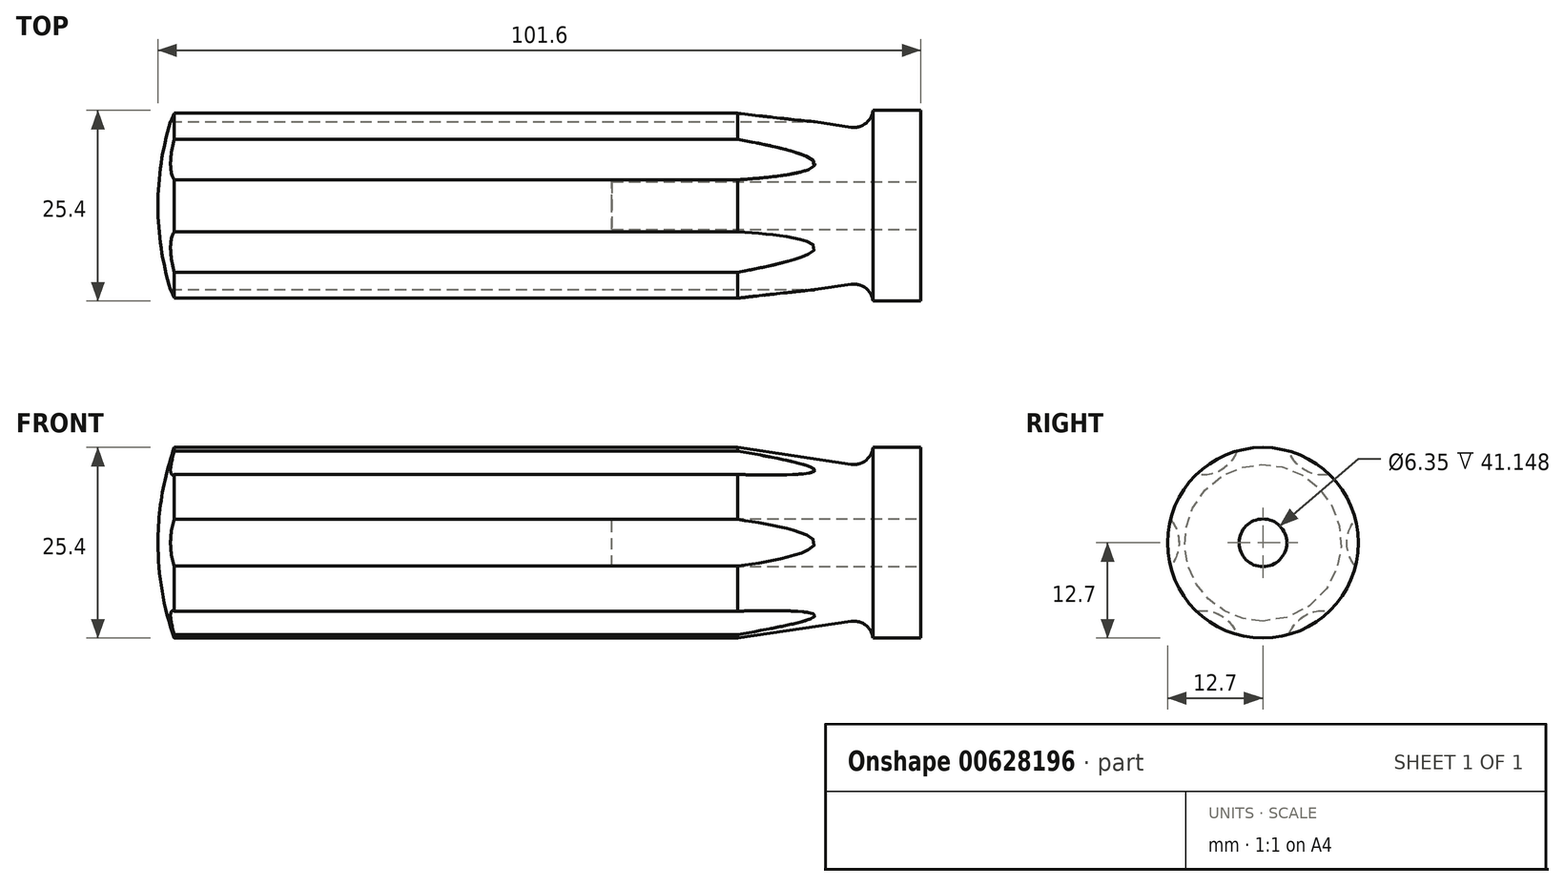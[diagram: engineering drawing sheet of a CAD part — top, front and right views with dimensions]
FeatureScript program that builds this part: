
annotation { "Feature Type Name" : "Feature", "Feature Type Description" : "" }
export const myFeature = defineFeature(function(context is Context, id is Id, definition is map)
    precondition{}
    {
        {
            var Q0;
            Q0=qCreatedBy(makeId("Front.planeOp"),FACE);
            var sketch = newSketch(context, id + "F0", { "sketchPlane" : qUnion([Q0])});
            skLineSegment(sketch, "E0", {"start": v(0, 0) * mm, "end": v(0, 12.7) * mm});
            skLineSegment(sketch, "E1", {"start": v(0, 12.7) * mm, "end": v(-6.35, 12.7) * mm});
            skLineSegment(sketch, "E2", {"start": v(-61, 12.7) * mm, "end": v(-69.88, 12.7) * mm});
            skLineSegment(sketch, "E3", {"start": v(-69.88, 12.7) * mm, "end": v(-100.1, 12.7) * mm});
            skLineSegment(sketch, "E4", {"start": v(-99.42, 12.7) * mm, "end": v(-100.1, 12.7) * mm});
            skLineSegment(sketch, "E5", {"start": v(0, 0) * mm, "end": v(-6.35, 0) * mm});
            skLineSegment(sketch, "E6", {"start": v(-6.35, 12.7) * mm, "end": v(-6.35, 12.7) * mm});
            skPoint(sketch, "E7.visualSharp", {"position": v(-6.35, 10.03) * mm});
            skArc(sketch, "E8", {"start": v(-99.42, 12.7) * mm, "mid": v(-101.05, 6.44) * mm, "end": v(-101.6, 0) * mm});
            skLineSegment(sketch, "E9", {"start": v(0, 0) * mm, "end": v(-101.6, 0) * mm});
            skLineSegment(sketch, "E10", {"start": v(-24.38, 12.7) * mm, "end": v(-33.27, 12.7) * mm});
            skLineSegment(sketch, "E11", {"start": v(-33.27, 12.7) * mm, "end": v(-61, 12.7) * mm});
            skLineSegment(sketch, "E12", {"start": v(-24.38, 12.7) * mm, "end": v(-9.26, 10.46) * mm});
            skArc(sketch, "E13.filletArc", {"start": v(-9.26, 10.46) * mm, "mid": v(-7.34, 10.97) * mm, "end": v(-6.37, 12.7) * mm});
            skLineSegment(sketch, "E14", {"start": v(-6.35, 12.7) * mm, "end": v(-6.37, 12.7) * mm});
            skSolve(sketch);
        }
        {
            var Q0;
            {var subQ1=sQuery(id+"F0.wireOp",EDGE,"E0");Q0=makeQuery(id+"F0.imprint","IMPRINT",FACE,{"disambiguationData":[TD([[makeQuery(id+"F0.imprint","IMPRINT",EDGE,{"derivedFrom":subQ1}),1.0]])]});}
            var Q1;
            Q1=sQuery(id+"F0.wireOp",EDGE,"E9");
            revolve(context, id + "F1", {"entities" : qUnion([Q0]), "axis" : qUnion([Q1]), "revolveType" : RevolveType.FULL});
        }
        {
            var Q0;
            Q0=qCreatedBy(makeId("Right.planeOp"),FACE);
            var sketch = newSketch(context, id + "F2", { "sketchPlane" : qUnion([Q0])});
            skLineSegment(sketch, "E15", {"start": v(0, 0) * mm, "end": v(20.05, 0) * mm, "construction": true});
            skLineSegment(sketch, "E16", {"start": v(0, 0) * mm, "end": v(-23.5, 0) * mm, "construction": true});
            skLineSegment(sketch, "E17", {"start": v(0, 0) * mm, "end": v(10.98, 19.02) * mm, "construction": true});
            skLineSegment(sketch, "E18", {"start": v(0, 0) * mm, "end": v(9.86, -17.07) * mm, "construction": true});
            skLineSegment(sketch, "E19", {"start": v(0, 0) * mm, "end": v(-10.6, -18.35) * mm, "construction": true});
            skLineSegment(sketch, "E20", {"start": v(0, 0) * mm, "end": v(-9.35, 16.2) * mm, "construction": true});
            skCircle(sketch, "E21", {"center": v(0, 0) * mm, "radius": 16 * mm, "construction": true});
            skCircle(sketch, "E22", {"center": v(8, 13.86) * mm, "radius": 4.83 * mm});
            skCircle(sketch, "E23", {"center": v(16, 0) * mm, "radius": 4.83 * mm});
            skCircle(sketch, "E24", {"center": v(8, -13.86) * mm, "radius": 4.83 * mm});
            skCircle(sketch, "E25", {"center": v(-8, -13.86) * mm, "radius": 4.83 * mm});
            skCircle(sketch, "E26", {"center": v(-8, 13.86) * mm, "radius": 4.83 * mm});
            skCircle(sketch, "E27", {"center": v(-16, 0) * mm, "radius": 4.83 * mm});
            skSolve(sketch);
        }
        {
            var Q0;
            Q0=makeQuery(id+"F2.imprint","IMPRINT",FACE,{"disambiguationData":[TD([[makeQuery(id+"F2.imprint","IMPRINT",EDGE,{"derivedFrom":sQuery(id+"F2.wireOp",EDGE,"E27")}),1.0]])]});
            var Q1;
            Q1=makeQuery(id+"F2.imprint","IMPRINT",FACE,{"disambiguationData":[TD([[makeQuery(id+"F2.imprint","IMPRINT",EDGE,{"derivedFrom":sQuery(id+"F2.wireOp",EDGE,"E26")}),1.0]])]});
            var Q2;
            Q2=makeQuery(id+"F2.imprint","IMPRINT",FACE,{"disambiguationData":[TD([[makeQuery(id+"F2.imprint","IMPRINT",EDGE,{"derivedFrom":sQuery(id+"F2.wireOp",EDGE,"E22")}),1.0]])]});
            var Q3;
            Q3=makeQuery(id+"F2.imprint","IMPRINT",FACE,{"disambiguationData":[TD([[makeQuery(id+"F2.imprint","IMPRINT",EDGE,{"derivedFrom":sQuery(id+"F2.wireOp",EDGE,"E23")}),1.0]])]});
            var Q4;
            Q4=makeQuery(id+"F2.imprint","IMPRINT",FACE,{"disambiguationData":[TD([[makeQuery(id+"F2.imprint","IMPRINT",EDGE,{"derivedFrom":sQuery(id+"F2.wireOp",EDGE,"E24")}),1.0]])]});
            var Q5;
            Q5=makeQuery(id+"F2.imprint","IMPRINT",FACE,{"disambiguationData":[TD([[makeQuery(id+"F2.imprint","IMPRINT",EDGE,{"derivedFrom":sQuery(id+"F2.wireOp",EDGE,"E25")}),1.0]])]});
            extrude(context, id + "F3", {"entities" : qUnion([Q0, Q1, Q2, Q3, Q4, Q5]), "operationType" : NewBodyOperationType.REMOVE, "oppositeDirection" : true, "depth" : 101.6 * mm, "offsetDistance" : 25.4 * mm, "hasSecondDirection" : true, "secondDirectionOppositeDirection" : true, "secondDirectionDepth" : 8.9 * mm});
        }
        {
            var Q0;
            Q0=qCreatedBy(makeId("Right.planeOp"),FACE);
            var sketch = newSketch(context, id + "F4", { "sketchPlane" : qUnion([Q0])});
            skCircle(sketch, "E28", {"center": v(0, 0) * mm, "radius": 3.18 * mm});
            skSolve(sketch);
        }
        {
            var Q0;
            Q0=makeQuery(id+"F4.imprint","IMPRINT",FACE,{"disambiguationData":[TD([[makeQuery(id+"F4.imprint","IMPRINT",EDGE,{"derivedFrom":sQuery(id+"F4.wireOp",EDGE,"E28")}),1.0]])]});
            extrude(context, id + "F5", {"entities" : qUnion([Q0]), "operationType" : NewBodyOperationType.REMOVE, "oppositeDirection" : true, "depth" : 41.15 * mm, "offsetDistance" : 25.4 * mm});
        }
    });
